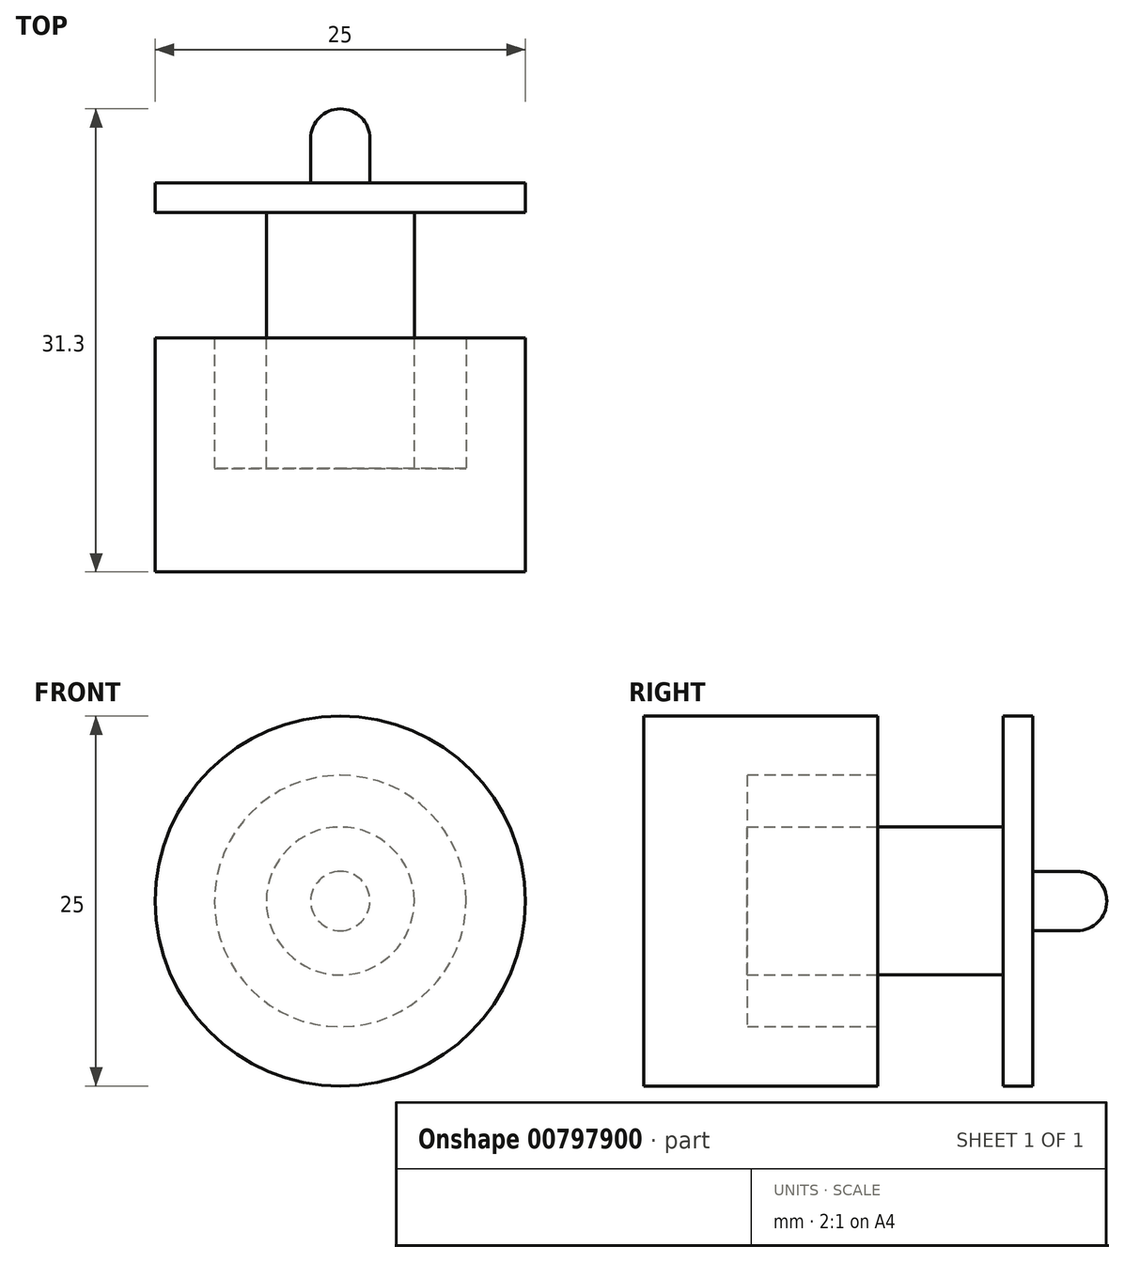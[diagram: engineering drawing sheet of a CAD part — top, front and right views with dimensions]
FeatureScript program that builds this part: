
annotation { "Feature Type Name" : "Feature", "Feature Type Description" : "" }
export const myFeature = defineFeature(function(context is Context, id is Id, definition is map)
    precondition{}
    {
        {
            var Q0;
            Q0=qCreatedBy(makeId("Front.planeOp"),FACE);
            var sketch = newSketch(context, id + "F0", { "sketchPlane" : qUnion([Q0])});
            skCircle(sketch, "E0", {"center": v(0, 0) * mm, "radius": 5 * mm});
            skSolve(sketch);
        }
        {
            var Q0;
            Q0 = qSketchRegion(id + "F0", true);
            extrude(context, id + "F1", {"entities" : qUnion([Q0]), "depth" : 17.3 * mm, "offsetDistance" : 25 * mm});
        }
        {
            var Q0;
            Q0=makeQuery(id+"F1.opExtrude","CAP_FACE",FACE,{"disambiguationData":[OSD([sQuery(id+"F0.wireOp",EDGE,"E0")])],"isStart":false});
            var sketch = newSketch(context, id + "F2", { "sketchPlane" : qUnion([Q0])});
            skCircle(sketch, "E1", {"center": v(0, 0) * mm, "radius": 12.5 * mm});
            skSolve(sketch);
        }
        {
            var Q0;
            Q0 = qSketchRegion(id + "F2", true);
            extrude(context, id + "F3", {"entities" : qUnion([Q0]), "operationType" : NewBodyOperationType.ADD, "depth" : 2 * mm, "offsetDistance" : 25 * mm});
        }
        {
            var Q0;
            Q0=makeQuery(id+"F3.opExtrude","CAP_FACE",FACE,{"disambiguationData":[OSD([sQuery(id+"F2.wireOp",EDGE,"E1")])],"isStart":true});
            var sketch = newSketch(context, id + "F4", { "sketchPlane" : qUnion([Q0])});
            skCircle(sketch, "E2", {"center": v(0, 0) * mm, "radius": 12.5 * mm});
            skCircle(sketch, "E3", {"center": v(0, 0) * mm, "radius": 8.5 * mm});
            skSolve(sketch);
        }
        {
            var Q0;
            Q0 = qSketchRegion(id + "F4", true);
            extrude(context, id + "F5", {"entities" : qUnion([Q0]), "operationType" : NewBodyOperationType.ADD, "depth" : 8.82 * mm, "offsetDistance" : 25 * mm});
        }
        {
            var Q0;
            Q0=makeQuery(id+"F1.opExtrude","CAP_FACE",FACE,{"disambiguationData":[OSD([sQuery(id+"F0.wireOp",EDGE,"E0")])],"isStart":true});
            var sketch = newSketch(context, id + "F6", { "sketchPlane" : qUnion([Q0])});
            skCircle(sketch, "E4", {"center": v(0, 0) * mm, "radius": 12.5 * mm});
            skSolve(sketch);
        }
        {
            var Q0;
            Q0 = qSketchRegion(id + "F6", true);
            extrude(context, id + "F7", {"entities" : qUnion([Q0]), "operationType" : NewBodyOperationType.ADD, "depth" : 2 * mm, "offsetDistance" : 25 * mm});
        }
        {
            var Q0;
            Q0=makeQuery(id+"F7.opExtrude","CAP_FACE",FACE,{"disambiguationData":[OSD([sQuery(id+"F6.wireOp",EDGE,"E4")])],"isStart":false});
            var sketch = newSketch(context, id + "F8", { "sketchPlane" : qUnion([Q0])});
            skCircle(sketch, "E5", {"center": v(0, 0) * mm, "radius": 2 * mm});
            skSolve(sketch);
        }
        {
            var Q0;
            Q0 = qSketchRegion(id + "F8", true);
            extrude(context, id + "F9", {"entities" : qUnion([Q0]), "operationType" : NewBodyOperationType.ADD, "depth" : 5 * mm, "offsetDistance" : 25 * mm});
        }
        {
            var Q0;
            Q0=makeQuery(id+"F9.opExtrude","CAP_EDGE",EDGE,{"disambiguationData":[OSD([sQuery(id+"F8.wireOp",EDGE,"E5")])],"isStart":false});
            fillet(context, id + "F10", {"entities" : qUnion([Q0]), "radius" : 2 * mm, "tangentPropagation" : true, "allowEdgeOverflow" : false});
        }
        {
            var Q0;
            Q0=makeQuery(id+"F3.opExtrude","CAP_FACE",FACE,{"disambiguationData":[OSD([sQuery(id+"F2.wireOp",EDGE,"E1")])],"isStart":false});
            var sketch = newSketch(context, id + "F11", { "sketchPlane" : qUnion([Q0])});
            skCircle(sketch, "E6", {"center": v(0, 0) * mm, "radius": 12.5 * mm});
            skSolve(sketch);
        }
        {
            var Q0;
            Q0 = qSketchRegion(id + "F11", true);
            extrude(context, id + "F12", {"entities" : qUnion([Q0]), "operationType" : NewBodyOperationType.ADD, "depth" : 5 * mm, "offsetDistance" : 25 * mm});
        }
    });
